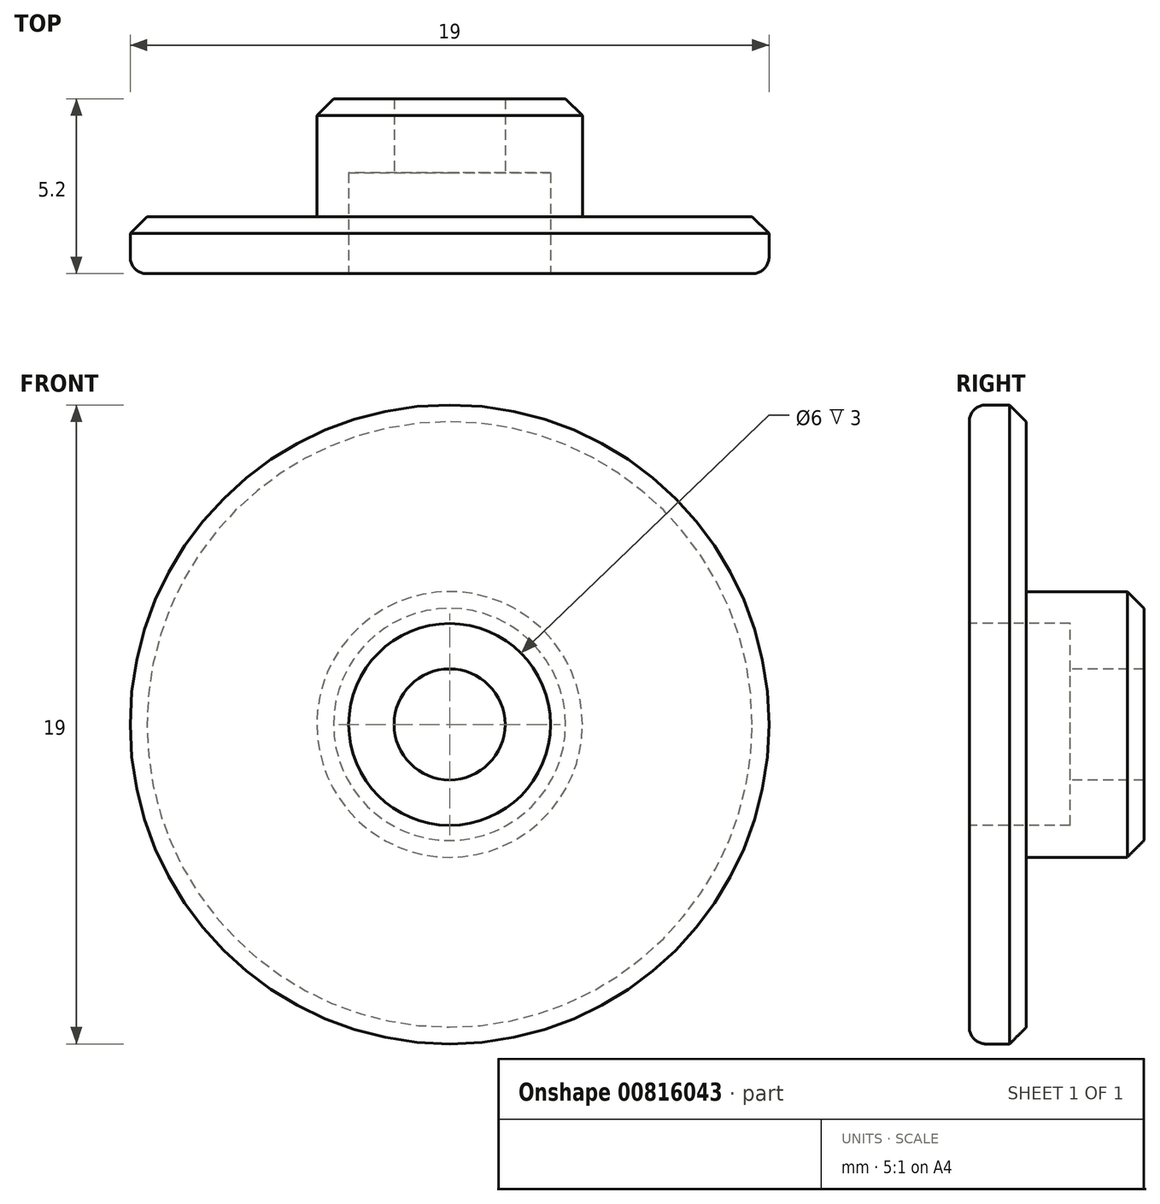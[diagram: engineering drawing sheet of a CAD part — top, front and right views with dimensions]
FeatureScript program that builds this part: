
annotation { "Feature Type Name" : "Feature", "Feature Type Description" : "" }
export const myFeature = defineFeature(function(context is Context, id is Id, definition is map)
    precondition{}
    {
        {
            var Q0;
            Q0=qCreatedBy(makeId("Front.planeOp"),FACE);
            var sketch = newSketch(context, id + "F0", { "sketchPlane" : qUnion([Q0])});
            skCircle(sketch, "E0", {"center": v(0, 0) * mm, "radius": 9.5 * mm});
            skSolve(sketch);
        }
        {
            var Q0;
            Q0 = qSketchRegion(id + "F0", true);
            extrude(context, id + "F1", {"entities" : qUnion([Q0]), "depth" : 1.7 * mm, "offsetDistance" : 25 * mm});
        }
        {
            var Q0;
            Q0=qCreatedBy(makeId("Front.planeOp"),FACE);
            var sketch = newSketch(context, id + "F2", { "sketchPlane" : qUnion([Q0])});
            skCircle(sketch, "E1", {"center": v(0, 0) * mm, "radius": 3.95 * mm});
            skSolve(sketch);
        }
        {
            var Q0;
            Q0 = qSketchRegion(id + "F2", true);
            extrude(context, id + "F3", {"entities" : qUnion([Q0]), "operationType" : NewBodyOperationType.ADD, "oppositeDirection" : true, "depth" : 3.5 * mm, "offsetDistance" : 25 * mm});
        }
        {
            var Q0;
            Q0=makeQuery(id+"F3.opExtrude","CAP_EDGE",EDGE,{"disambiguationData":[OSD([sQuery(id+"F2.wireOp",EDGE,"E1")])],"isStart":false});
            var Q1;
            Q1=makeQuery(id+"F1.opExtrude","CAP_EDGE",EDGE,{"disambiguationData":[OSD([sQuery(id+"F0.wireOp",EDGE,"E0")])],"isStart":true});
            chamfer(context, id + "F4", {"entities" : qUnion([Q0, Q1]), "width" : 0.5 * mm, "tangentPropagation" : true});
        }
        {
            var Q0;
            Q0=makeQuery(id+"F1.opExtrude","CAP_EDGE",EDGE,{"disambiguationData":[OSD([sQuery(id+"F0.wireOp",EDGE,"E0")])],"isStart":false});
            fillet(context, id + "F5", {"entities" : qUnion([Q0]), "radius" : 0.5 * mm, "tangentPropagation" : true, "allowEdgeOverflow" : false});
        }
        {
            var Q0;
            Q0=makeQuery(id+"F1.opExtrude","CAP_FACE",FACE,{"disambiguationData":[OSD([sQuery(id+"F0.wireOp",EDGE,"E0")])],"isStart":false});
            var sketch = newSketch(context, id + "F6", { "sketchPlane" : qUnion([Q0])});
            skPoint(sketch, "E2", {"position": v(0, 0) * mm});
            skSolve(sketch);
        }
        {
            var Q0;
            Q0=sQuery(id+"F6.wireOp",VERTEX,"E2");
            var Q1;
            Q1=makeQuery(id+"F1.opExtrude","SWEPT_BODY",BODY,{"disambiguationData":[OSD([sQuery(id+"F0.wireOp",EDGE,"E0")])]});
            hole(context, id + "F7", {"style" : HoleStyle.C_BORE, "endStyle" : HoleEndStyle.THROUGH, "holeDiameter" : 3.3 * mm, "cBoreDiameter" : 6 * mm, "cBoreDepth" : 3 * mm, "majorDiameter" : 3 * mm, "isTappedThrough" : true, "tappedDepth" : 27 * mm, "tapClearance" : 3, "locations" : qUnion([Q0]), "scope" : qUnion([Q1])});
        }
    });
